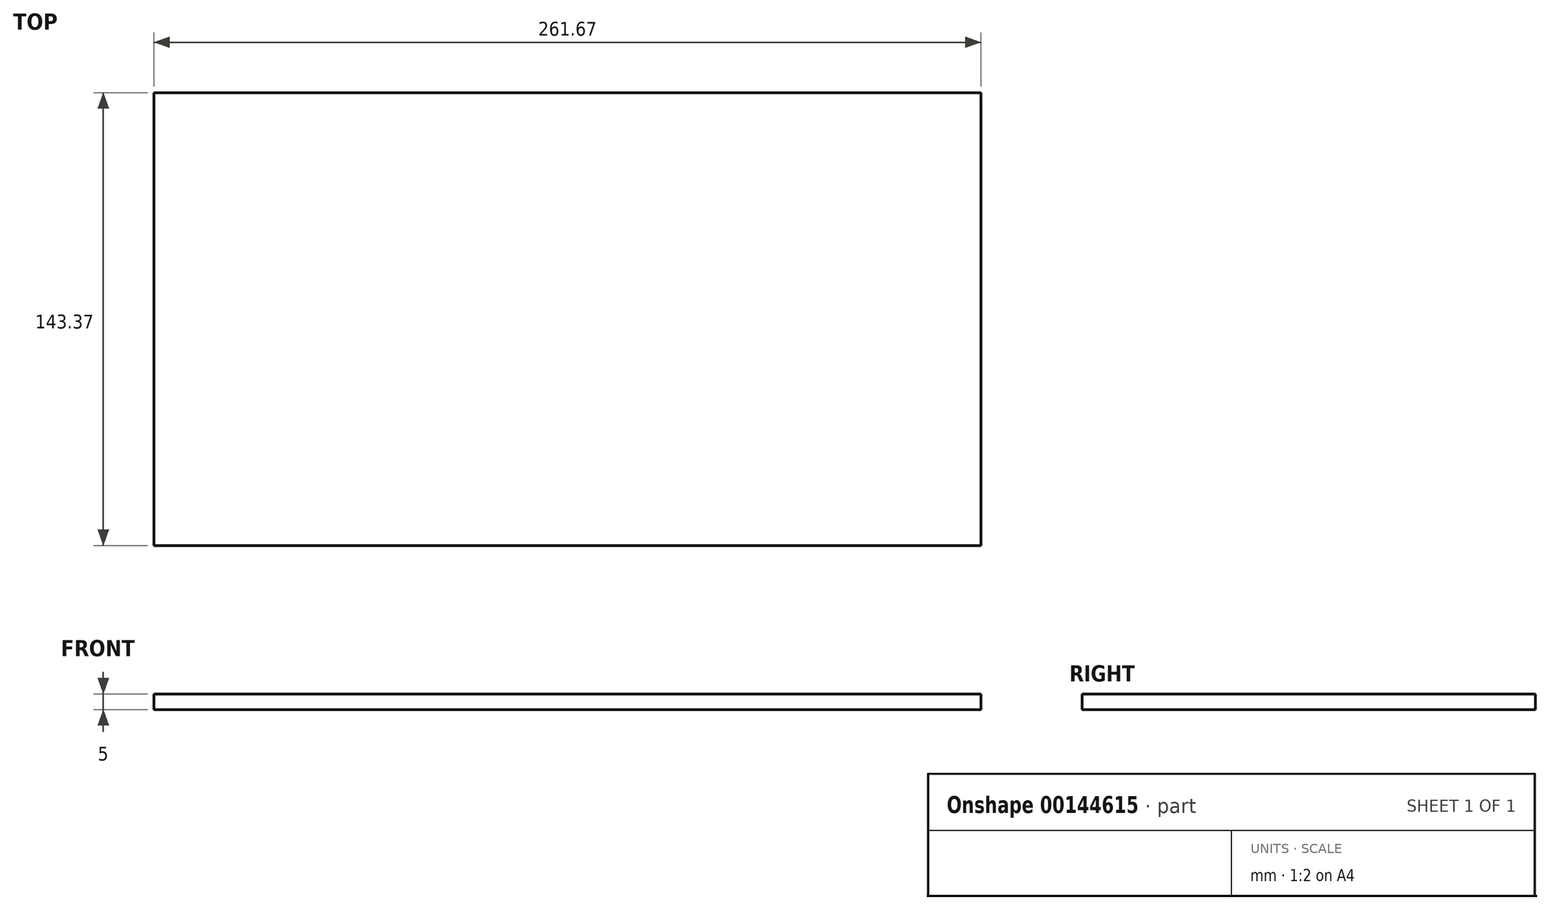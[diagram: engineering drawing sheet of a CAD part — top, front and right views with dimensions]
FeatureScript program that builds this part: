
annotation { "Feature Type Name" : "Feature", "Feature Type Description" : "" }
export const myFeature = defineFeature(function(context is Context, id is Id, definition is map)
    precondition{}
    {
        {
            var Q0;
            Q0=qCreatedBy(makeId("Top.planeOp"),FACE);
            var sketch = newSketch(context, id + "F0", { "sketchPlane" : qUnion([Q0])});
            skLineSegment(sketch, "E0.bottom", {"start": v(-142.12, 60.55) * mm, "end": v(119.55, 60.55) * mm});
            skLineSegment(sketch, "E0.top", {"start": v(-142.12, -82.82) * mm, "end": v(119.55, -82.82) * mm});
            skLineSegment(sketch, "E0.left", {"start": v(-142.12, 60.55) * mm, "end": v(-142.12, -82.82) * mm});
            skLineSegment(sketch, "E0.right", {"start": v(119.55, 60.55) * mm, "end": v(119.55, -82.82) * mm});
            skSolve(sketch);
        }
        {
            var Q0;
            Q0=makeQuery(id+"F0.imprint","IMPRINT",FACE,{"disambiguationData":[TD([[makeQuery(id+"F0.imprint","IMPRINT",EDGE,{"derivedFrom":sQuery(id+"F0.wireOp",EDGE,"E0.bottom")}),-1.0]])]});
            extrude(context, id + "F1", {"entities" : qUnion([Q0]), "depth" : 5 * mm});
        }
    });
